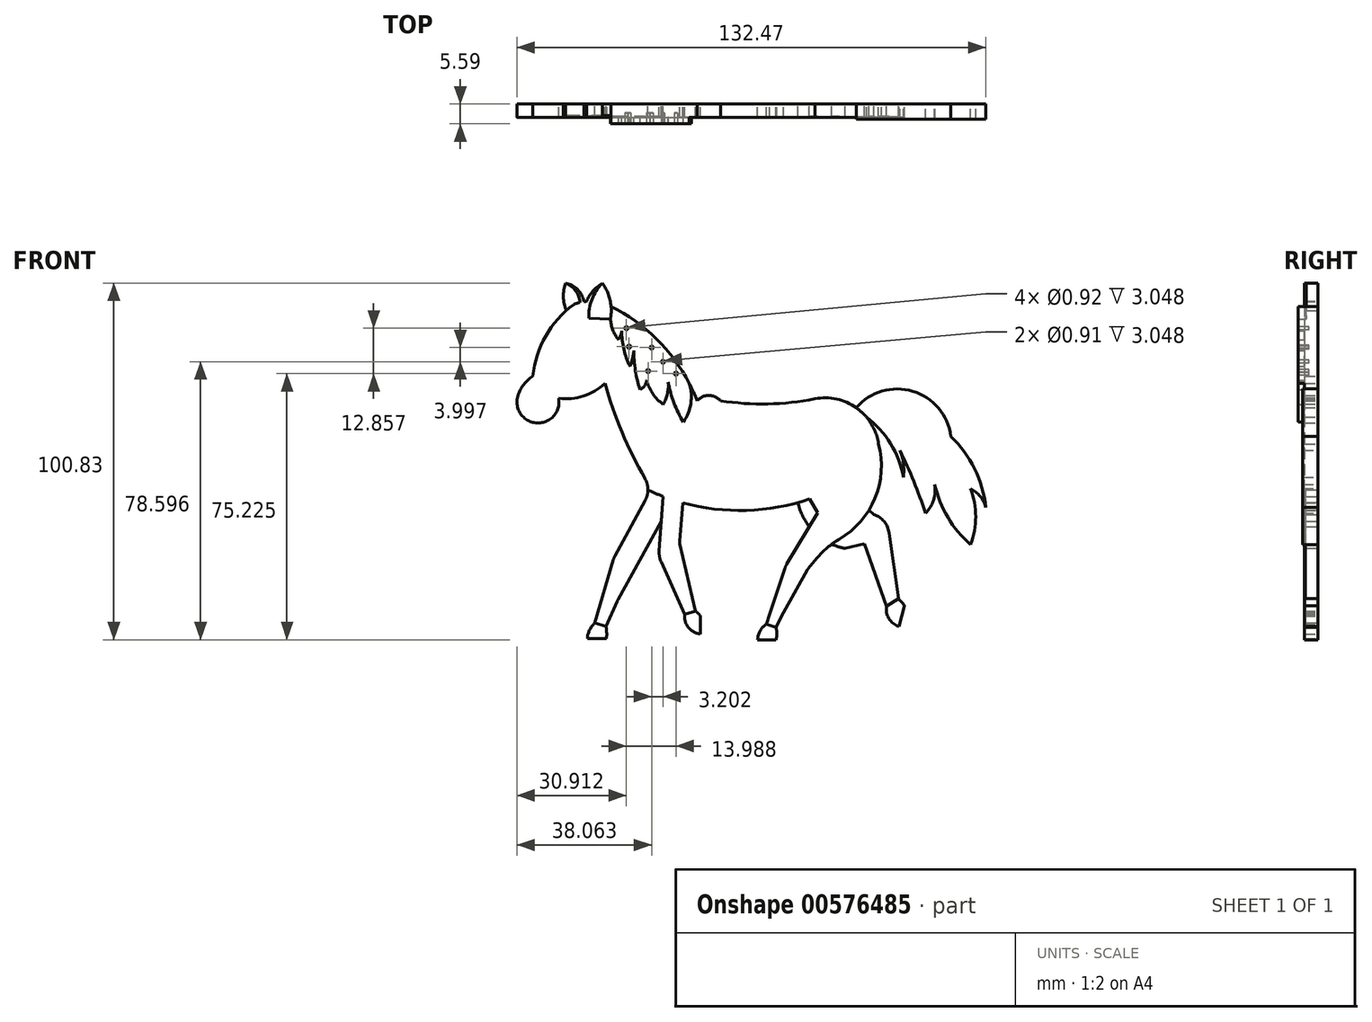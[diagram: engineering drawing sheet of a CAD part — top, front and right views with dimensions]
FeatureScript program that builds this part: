
annotation { "Feature Type Name" : "Feature", "Feature Type Description" : "" }
export const myFeature = defineFeature(function(context is Context, id is Id, definition is map)
    precondition{}
    {
        {
            var Q0;
            Q0=qCreatedBy(makeId("Front.planeOp"),FACE);
            var sketch = newSketch(context, id + "F0", { "sketchPlane" : qUnion([Q0])});
            skArc(sketch, "E0", {"start": v(-28.5, 3.23) * mm, "mid": v(-38.16, 18.83) * mm, "end": v(-52.8, 29.89) * mm});
            skArc(sketch, "E1", {"start": v(-21.88, 3.23) * mm, "mid": v(-25.19, 4.74) * mm, "end": v(-28.5, 3.23) * mm});
            skArc(sketch, "E2", {"start": v(-21.88, 3.23) * mm, "mid": v(-8.5, 2.33) * mm, "end": v(4.81, 3.8) * mm});
            skPoint(sketch, "E3.visualSharp", {"position": v(-35.88, -8.64) * mm});
            skArc(sketch, "E3.filletArc", {"start": v(-35.17, -11.7) * mm, "mid": v(-35.18, -11.7) * mm, "end": v(-35.18, -11.68) * mm});
            skPoint(sketch, "E4.visualSharp", {"position": v(-34.53, -14.51) * mm});
            skPoint(sketch, "E5.visualSharp", {"position": v(-52.4, -44.17) * mm});
            skPoint(sketch, "E6.visualSharp", {"position": v(-50.96, -53.17) * mm});
            skPoint(sketch, "E7.visualSharp", {"position": v(-50.4, -54.66) * mm});
            skPoint(sketch, "E8.visualSharp", {"position": v(-57.39, -59.58) * mm});
            skPoint(sketch, "E9.orphan", {"position": v(-27.47, -12) * mm});
            skArc(sketch, "E10", {"start": v(-67.62, 3.94) * mm, "mid": v(-57.44, 5.94) * mm, "end": v(-50.7, 13.82) * mm});
            skArc(sketch, "E11", {"start": v(-79.34, 3.55) * mm, "mid": v(-73.25, -3.06) * mm, "end": v(-67.62, 3.94) * mm});
            skArc(sketch, "E12", {"start": v(-74.9, 10.2) * mm, "mid": v(-77.82, 7.35) * mm, "end": v(-79.34, 3.55) * mm});
            skArc(sketch, "E13", {"start": v(-59.7, 31.32) * mm, "mid": v(-61.6, 31.02) * mm, "end": v(-63.44, 30.42) * mm});
            skArc(sketch, "E14", {"start": v(-63.44, 30.42) * mm, "mid": v(-71.29, 21.51) * mm, "end": v(-74.9, 10.2) * mm});
            skPoint(sketch, "E15.startSnap0", {"position": v(-57.44, 5.94) * mm});
            skArc(sketch, "E16", {"start": v(-43.23, -18.78) * mm, "mid": v(-49.7, -5.68) * mm, "end": v(-54.55, 8.11) * mm});
            skLineSegment(sketch, "E17", {"start": v(-43.16, -24.96) * mm, "end": v(-51.67, -40.58) * mm});
            skLineSegment(sketch, "E18", {"start": v(-52.18, -41.83) * mm, "end": v(-57.39, -59.58) * mm});
            skLineSegment(sketch, "E19", {"start": v(-38.6, -30.9) * mm, "end": v(-50.82, -52.92) * mm});
            skLineSegment(sketch, "E20", {"start": v(-51.07, -53.43) * mm, "end": v(-54.22, -60.52) * mm});
            skArc(sketch, "E21", {"start": v(-57.39, -59.58) * mm, "mid": v(-58.88, -61.57) * mm, "end": v(-59.5, -63.97) * mm});
            skLineSegment(sketch, "E22", {"start": v(-59.5, -63.97) * mm, "end": v(-54.08, -63.97) * mm});
            skArc(sketch, "E23", {"start": v(-54.08, -63.97) * mm, "mid": v(-54.05, -62.24) * mm, "end": v(-54.22, -60.52) * mm});
            skPoint(sketch, "E24.visualSharp", {"position": v(-51.99, -41.18) * mm});
            skArc(sketch, "E24.filletArc", {"start": v(-51.67, -40.58) * mm, "mid": v(-51.96, -41.2) * mm, "end": v(-52.18, -41.83) * mm});
            skArc(sketch, "E25.filletArc", {"start": v(-50.82, -52.92) * mm, "mid": v(-50.95, -53.17) * mm, "end": v(-51.07, -53.43) * mm});
            skPoint(sketch, "E26.visualSharp", {"position": v(-31.52, -18.16) * mm});
            skPoint(sketch, "E27.visualSharp", {"position": v(-41.44, -21.8) * mm});
            skArc(sketch, "E27.filletArc", {"start": v(-43.16, -24.96) * mm, "mid": v(-42.4, -21.86) * mm, "end": v(-43.23, -18.78) * mm});
            skArc(sketch, "E28", {"start": v(22.78, -8.96) * mm, "mid": v(16.5, 1.23) * mm, "end": v(4.81, 3.8) * mm});
            skArc(sketch, "E29", {"start": v(-42.4, -22) * mm, "mid": v(-40.25, -22.95) * mm, "end": v(-38.08, -23.82) * mm});
            skPoint(sketch, "E29.startSnap0", {"position": v(-42.4, -21.86) * mm});
            skLineSegment(sketch, "E30", {"start": v(-38.66, -42.3) * mm, "end": v(-32.03, -57.1) * mm});
            skLineSegment(sketch, "E31", {"start": v(-39.2, -39.25) * mm, "end": v(-38.08, -23.82) * mm});
            skArc(sketch, "E32.trimOffspring", {"start": v(-32.57, -25.62) * mm, "mid": v(-14.58, -27.77) * mm, "end": v(3.25, -24.53) * mm});
            skLineSegment(sketch, "E33", {"start": v(-32.57, -25.62) * mm, "end": v(-33.35, -36.4) * mm});
            skArc(sketch, "E34", {"start": v(-40.07, -8.18) * mm, "mid": v(-40.8, -16.22) * mm, "end": v(-38.08, -23.82) * mm});
            skArc(sketch, "E35", {"start": v(-32.57, -25.62) * mm, "mid": v(-31.52, -18.16) * mm, "end": v(-33.38, -10.86) * mm});
            skPoint(sketch, "E36.visualSharp", {"position": v(-39.32, -40.85) * mm});
            skArc(sketch, "E36.filletArc", {"start": v(-39.2, -39.25) * mm, "mid": v(-39.12, -40.81) * mm, "end": v(-38.66, -42.3) * mm});
            skPoint(sketch, "E37.visualSharp", {"position": v(-33.67, -40.85) * mm});
            skArc(sketch, "E37.filletArc", {"start": v(-33.35, -36.4) * mm, "mid": v(-33.37, -36.82) * mm, "end": v(-33.36, -37.24) * mm});
            skLineSegment(sketch, "E38", {"start": v(-28.96, -56.23) * mm, "end": v(-33.36, -37.24) * mm});
            skArc(sketch, "E39", {"start": v(-32.03, -57.1) * mm, "mid": v(-30.95, -60.84) * mm, "end": v(-27.52, -62.7) * mm});
            skLineSegment(sketch, "E40", {"start": v(-27.52, -62.7) * mm, "end": v(-27.52, -57.67) * mm});
            skArc(sketch, "E41", {"start": v(-27.52, -57.67) * mm, "mid": v(-28.18, -56.9) * mm, "end": v(-28.96, -56.23) * mm});
            skArc(sketch, "E42", {"start": v(-55.24, 36.49) * mm, "mid": v(-58.22, 31.92) * mm, "end": v(-59.04, 26.52) * mm});
            skPoint(sketch, "E43.orphan", {"position": v(-53.9, 30.42) * mm});
            skPoint(sketch, "E44.start.orphan", {"position": v(-52.24, 26.52) * mm});
            skArc(sketch, "E45", {"start": v(-52.98, 26.32) * mm, "mid": v(-53.07, 31.63) * mm, "end": v(-55.24, 36.49) * mm});
            skArc(sketch, "E46", {"start": v(-55.24, 36.49) * mm, "mid": v(-59.27, 32.24) * mm, "end": v(-60.51, 26.52) * mm});
            skArc(sketch, "E47", {"start": v(-61.6, 31.02) * mm, "mid": v(-62.84, 34.36) * mm, "end": v(-65.7, 36.49) * mm});
            skArc(sketch, "E48", {"start": v(-65.7, 36.49) * mm, "mid": v(-66.27, 32.6) * mm, "end": v(-65.46, 28.77) * mm});
            skArc(sketch, "E49", {"start": v(-60.51, 31.23) * mm, "mid": v(-62.26, 34.7) * mm, "end": v(-65.7, 36.49) * mm});
            skArc(sketch, "E50", {"start": v(5.3, 0) * mm, "mid": v(-0.54, -10.33) * mm, "end": v(1.75, -21.97) * mm});
            skLineSegment(sketch, "E51", {"start": v(5.36, -41.27) * mm, "end": v(2.9, -44.2) * mm});
            skLineSegment(sketch, "E52", {"start": v(2.68, -44.54) * mm, "end": v(-4.1, -56.69) * mm});
            skPoint(sketch, "E53.end.orphan", {"position": v(-8.88, -61.12) * mm});
            skPoint(sketch, "E53.start.orphan", {"position": v(-5.3, -56.69) * mm});
            skPoint(sketch, "E54.end.orphan", {"position": v(0, -44.36) * mm});
            skArc(sketch, "E55", {"start": v(11.65, -35.94) * mm, "mid": v(21.75, -24.32) * mm, "end": v(22.78, -8.96) * mm});
            skPoint(sketch, "E56.visualSharp", {"position": v(-2.59, -44.36) * mm});
            skPoint(sketch, "E57.visualSharp", {"position": v(2.78, -44.36) * mm});
            skArc(sketch, "E57.filletArc", {"start": v(2.9, -44.2) * mm, "mid": v(2.79, -44.37) * mm, "end": v(2.68, -44.54) * mm});
            skPoint(sketch, "E58.visualSharp", {"position": v(8.52, -37.48) * mm});
            skArc(sketch, "E58.filletArc", {"start": v(11.65, -35.94) * mm, "mid": v(8.27, -38.33) * mm, "end": v(5.36, -41.27) * mm});
            skPoint(sketch, "E59.visualSharp", {"position": v(9.47, -28.7) * mm});
            skPoint(sketch, "E60.visualSharp", {"position": v(-7.2, -56.69) * mm});
            skLineSegment(sketch, "E61", {"start": v(-6.19, -64.34) * mm, "end": v(-11.38, -64.34) * mm});
            skLineSegment(sketch, "E62", {"start": v(5.52, -28.42) * mm, "end": v(-3.13, -42.91) * mm});
            skLineSegment(sketch, "E63", {"start": v(-3.7, -44.17) * mm, "end": v(-8, -57.1) * mm});
            skPoint(sketch, "E56.filletArc.start.orphan", {"position": v(-1.93, -43.5) * mm});
            skPoint(sketch, "E64.visualSharp", {"position": v(-3.49, -43.5) * mm});
            skArc(sketch, "E64.filletArc", {"start": v(-3.13, -42.91) * mm, "mid": v(-3.45, -43.53) * mm, "end": v(-3.7, -44.17) * mm});
            skArc(sketch, "E65", {"start": v(-8.87, -59.93) * mm, "mid": v(-10.7, -61.8) * mm, "end": v(-11.38, -64.34) * mm});
            skArc(sketch, "E66", {"start": v(-6.2, -64.37) * mm, "mid": v(-5.95, -62.6) * mm, "end": v(-6.2, -60.82) * mm});
            skLineSegment(sketch, "E67", {"start": v(-8, -57.1) * mm, "end": v(-8.87, -59.93) * mm});
            skLineSegment(sketch, "E68", {"start": v(-6.2, -60.82) * mm, "end": v(-4.1, -56.69) * mm});
            skPoint(sketch, "E69.orphan", {"position": v(-3.18, -64.34) * mm});
            skLineSegment(sketch, "E70", {"start": v(1.75, -21.97) * mm, "end": v(5.52, -28.42) * mm});
            skPoint(sketch, "E71.orphan", {"position": v(5.52, -23.7) * mm});
            skArc(sketch, "E72", {"start": v(0, -25.54) * mm, "mid": v(1.2, -29.11) * mm, "end": v(3.18, -32.33) * mm});
            skArc(sketch, "E73.trimOffspring", {"start": v(9.55, -37.32) * mm, "mid": v(11.43, -38.04) * mm, "end": v(13.38, -38.52) * mm});
            skLineSegment(sketch, "E74", {"start": v(13.38, -38.52) * mm, "end": v(18.78, -37.2) * mm});
            skLineSegment(sketch, "E75", {"start": v(18.78, -37.2) * mm, "end": v(25.01, -54.82) * mm});
            skLineSegment(sketch, "E76", {"start": v(25.76, -34.1) * mm, "end": v(28.38, -52.73) * mm});
            skPoint(sketch, "E77.visualSharp", {"position": v(25.18, -29.96) * mm});
            skArc(sketch, "E77.filletArc", {"start": v(25.76, -34.1) * mm, "mid": v(24.35, -30.9) * mm, "end": v(21.46, -28.95) * mm});
            skLineSegment(sketch, "E78", {"start": v(21.46, -28.95) * mm, "end": v(20.03, -27.7) * mm});
            skArc(sketch, "E79", {"start": v(25.01, -54.82) * mm, "mid": v(25.7, -58.34) * mm, "end": v(28.51, -60.57) * mm});
            skLineSegment(sketch, "E80", {"start": v(28.51, -60.57) * mm, "end": v(30.16, -54.78) * mm});
            skArc(sketch, "E81", {"start": v(30.16, -54.78) * mm, "mid": v(29.33, -53.7) * mm, "end": v(28.38, -52.73) * mm});
            skLineSegment(sketch, "E82", {"start": v(-57.39, -59.58) * mm, "end": v(-54.22, -60.52) * mm});
            skLineSegment(sketch, "E83", {"start": v(-32.03, -57.1) * mm, "end": v(-28.96, -56.23) * mm});
            skLineSegment(sketch, "E84", {"start": v(-8.87, -59.93) * mm, "end": v(-6.2, -60.82) * mm});
            skLineSegment(sketch, "E85", {"start": v(25.01, -54.82) * mm, "end": v(28.38, -52.73) * mm});
            skLineSegment(sketch, "E86", {"start": v(-60.51, 26.52) * mm, "end": v(-59.04, 26.52) * mm});
            skLineSegment(sketch, "E87", {"start": v(-59.04, 26.52) * mm, "end": v(-52.98, 26.32) * mm});
            skArc(sketch, "E88", {"start": v(-52.98, 26.32) * mm, "mid": v(-52.3, 23.22) * mm, "end": v(-50.7, 20.49) * mm});
            skArc(sketch, "E89", {"start": v(-50.7, 20.49) * mm, "mid": v(-50.12, 21.68) * mm, "end": v(-49.78, 22.95) * mm});
            skArc(sketch, "E90", {"start": v(-49.78, 22.95) * mm, "mid": v(-49.2, 17.8) * mm, "end": v(-47.43, 12.93) * mm});
            skArc(sketch, "E91", {"start": v(-47.43, 12.93) * mm, "mid": v(-46.75, 15.12) * mm, "end": v(-46.37, 17.38) * mm});
            skArc(sketch, "E92", {"start": v(-46.37, 17.38) * mm, "mid": v(-45.93, 11.82) * mm, "end": v(-44.62, 6.4) * mm});
            skArc(sketch, "E93", {"start": v(-42.74, 9.07) * mm, "mid": v(-41.03, 5.23) * mm, "end": v(-38.1, 2.22) * mm});
            skArc(sketch, "E94", {"start": v(-38.1, 2.22) * mm, "mid": v(-36.86, 5.28) * mm, "end": v(-36.68, 8.58) * mm});
            skArc(sketch, "E95", {"start": v(-36.68, 8.58) * mm, "mid": v(-35.06, 2.68) * mm, "end": v(-32.37, -2.82) * mm});
            skArc(sketch, "E96", {"start": v(-32.37, -2.82) * mm, "mid": v(-30.27, 2.45) * mm, "end": v(-30.7, 8.1) * mm});
            skArc(sketch, "E97", {"start": v(-44.62, 6.4) * mm, "mid": v(-43.31, 7.48) * mm, "end": v(-42.74, 9.07) * mm});
            skArc(sketch, "E98", {"start": v(29.78, -18.35) * mm, "mid": v(29.81, -14.53) * mm, "end": v(28.82, -10.84) * mm});
            skArc(sketch, "E99", {"start": v(36.04, -28.56) * mm, "mid": v(32.74, -19.57) * mm, "end": v(28.82, -10.84) * mm});
            skArc(sketch, "E100", {"start": v(36.04, -28.56) * mm, "mid": v(38.32, -24.84) * mm, "end": v(38.66, -20.48) * mm});
            skArc(sketch, "E101", {"start": v(38.66, -20.48) * mm, "mid": v(42.37, -29.75) * mm, "end": v(48.75, -37.42) * mm});
            skArc(sketch, "E102", {"start": v(48.75, -37.42) * mm, "mid": v(50.24, -29.53) * mm, "end": v(48.75, -21.63) * mm});
            skArc(sketch, "E103", {"start": v(53.09, -26.92) * mm, "mid": v(51.5, -23.8) * mm, "end": v(48.75, -21.63) * mm});
            skArc(sketch, "E104", {"start": v(43.17, -6.8) * mm, "mid": v(32.45, 5.91) * mm, "end": v(16.5, 1.23) * mm});
            skArc(sketch, "E105", {"start": v(53.09, -26.92) * mm, "mid": v(49.91, -15.98) * mm, "end": v(43.17, -6.8) * mm});
            skArc(sketch, "E106", {"start": v(29.78, -18.35) * mm, "mid": v(26.21, -8.88) * mm, "end": v(19.36, -1.41) * mm});
            skCircle(sketch, "E107", {"center": v(5.22, 54.47) * mm, "radius": 8.7 * mm});
            skSolve(sketch);
        }
        {
            var Q0;
            Q0=makeQuery(id+"F0.imprint","IMPRINT",FACE,{"disambiguationData":[TD([[makeQuery(id+"F0.imprint","IMPRINT",EDGE,{"derivedFrom":sQuery(id+"F0.wireOp",EDGE,"E21")}),1.0]])]});
            extrude(context, id + "F1", {"entities" : qUnion([Q0]), "depth" : 3.8 * mm, "offsetDistance" : 25.4 * mm});
        }
        {
            var Q0;
            Q0=makeQuery(id+"F0.imprint","IMPRINT",FACE,{"disambiguationData":[TD([[makeQuery(id+"F0.imprint","IMPRINT",EDGE,{"derivedFrom":sQuery(id+"F0.wireOp",EDGE,"E39")}),1.0]])]});
            extrude(context, id + "F2", {"entities" : qUnion([Q0]), "depth" : 3.8 * mm, "offsetDistance" : 25.4 * mm});
        }
        {
            var Q0;
            {var subQ0=sQuery(id+"F0.wireOp",EDGE,"E61");Q0=makeQuery(id+"F0.imprint","IMPRINT",FACE,{"disambiguationData":[TD([[makeQuery(id+"F0.imprint","IMPRINT",EDGE,{"derivedFrom":subQ0}),-1.0]])]});}
            extrude(context, id + "F3", {"entities" : qUnion([Q0]), "depth" : 3.8 * mm, "offsetDistance" : 25.4 * mm});
        }
        {
            var Q0;
            Q0=makeQuery(id+"F0.imprint","IMPRINT",FACE,{"disambiguationData":[TD([[makeQuery(id+"F0.imprint","IMPRINT",EDGE,{"derivedFrom":sQuery(id+"F0.wireOp",EDGE,"E79")}),1.0]])]});
            extrude(context, id + "F4", {"entities" : qUnion([Q0]), "depth" : 3.8 * mm, "offsetDistance" : 25.4 * mm});
        }
        {
            var Q0;
            {var subQ0=sQuery(id+"F0.wireOp",EDGE,"E73.trimOffspring");Q0=makeQuery(id+"F0.imprint","IMPRINT",FACE,{"disambiguationData":[TD([[makeQuery(id+"F0.imprint","IMPRINT",EDGE,{"derivedFrom":subQ0}),1.0]])]});}
            extrude(context, id + "F5", {"entities" : qUnion([Q0]), "operationType" : NewBodyOperationType.ADD, "depth" : 3.56 * mm, "offsetDistance" : 25.4 * mm});
        }
        {
            var Q0;
            {var subQ2=sQuery(id+"F0.wireOp",EDGE,"E17");Q0=makeQuery(id+"F0.imprint","IMPRINT",FACE,{"disambiguationData":[TD([[makeQuery(id+"F0.imprint","IMPRINT",EDGE,{"derivedFrom":subQ2}),1.0]])]});}
            extrude(context, id + "F6", {"entities" : qUnion([Q0]), "depth" : 3.56 * mm, "offsetDistance" : 25.4 * mm});
        }
        {
            var Q0;
            {var subQ32=sQuery(id+"F0.wireOp",EDGE,"E1");Q0=makeQuery(id+"F0.imprint","IMPRINT",FACE,{"disambiguationData":[TD([[makeQuery(id+"F0.imprint","IMPRINT",EDGE,{"derivedFrom":subQ32}),1.0]])]});}
            extrude(context, id + "F7", {"entities" : qUnion([Q0]), "depth" : 3.8 * mm, "offsetDistance" : 25.4 * mm});
        }
        {
            var Q0;
            {var subQ0=sQuery(id+"F0.wireOp",EDGE,"E47");Q0=makeQuery(id+"F0.imprint","IMPRINT",FACE,{"disambiguationData":[TD([[makeQuery(id+"F0.imprint","IMPRINT",EDGE,{"derivedFrom":subQ0}),-1.0]])]});}
            extrude(context, id + "F8", {"entities" : qUnion([Q0]), "operationType" : NewBodyOperationType.ADD, "depth" : 3.8 * mm, "offsetDistance" : 25.4 * mm});
        }
        {
            var Q0;
            {var subQ0=sQuery(id+"F0.wireOp",EDGE,"E42");Q0=makeQuery(id+"F0.imprint","IMPRINT",FACE,{"disambiguationData":[TD([[makeQuery(id+"F0.imprint","IMPRINT",EDGE,{"derivedFrom":subQ0}),-1.0]])]});}
            extrude(context, id + "F9", {"entities" : qUnion([Q0]), "operationType" : NewBodyOperationType.ADD, "depth" : 3.8 * mm, "offsetDistance" : 25.4 * mm});
        }
        {
            var Q0;
            {var subQ3=sQuery(id+"F0.wireOp",EDGE,"E47");Q0=makeQuery(id+"F0.imprint","IMPRINT",FACE,{"disambiguationData":[TD([[makeQuery(id+"F0.imprint","IMPRINT",EDGE,{"derivedFrom":subQ3}),1.0]])]});}
            extrude(context, id + "F10", {"entities" : qUnion([Q0]), "operationType" : NewBodyOperationType.ADD, "depth" : 3.3 * mm, "offsetDistance" : 25.4 * mm});
        }
        {
            var Q0;
            {var subQ0=sQuery(id+"F0.wireOp",EDGE,"E42");Q0=makeQuery(id+"F0.imprint","IMPRINT",FACE,{"disambiguationData":[TD([[makeQuery(id+"F0.imprint","IMPRINT",EDGE,{"derivedFrom":subQ0}),1.0]])]});}
            extrude(context, id + "F11", {"entities" : qUnion([Q0]), "operationType" : NewBodyOperationType.ADD, "depth" : 3.3 * mm, "offsetDistance" : 25.4 * mm});
        }
        {
            var Q0;
            {var subQ3=sQuery(id+"F0.wireOp",EDGE,"E72");Q0=makeQuery(id+"F0.imprint","IMPRINT",FACE,{"disambiguationData":[TD([[makeQuery(id+"F0.imprint","IMPRINT",EDGE,{"derivedFrom":subQ3}),1.0]])]});}
            extrude(context, id + "F12", {"entities" : qUnion([Q0]), "operationType" : NewBodyOperationType.ADD, "depth" : 3.56 * mm, "offsetDistance" : 25.4 * mm});
        }
        {
            var Q0;
            {var subQ3=sQuery(id+"F0.wireOp",EDGE,"E88");Q0=makeQuery(id+"F0.imprint","IMPRINT",FACE,{"disambiguationData":[TD([[makeQuery(id+"F0.imprint","IMPRINT",EDGE,{"derivedFrom":subQ3}),1.0]])]});}
            extrude(context, id + "F13", {"entities" : qUnion([Q0]), "operationType" : NewBodyOperationType.ADD, "depth" : 5.6 * mm, "offsetDistance" : 25.4 * mm});
        }
        {
            var Q0;
            Q0=makeQuery(id+"F0.imprint","IMPRINT",FACE,{"disambiguationData":[TD([[makeQuery(id+"F0.imprint","IMPRINT",EDGE,{"derivedFrom":sQuery(id+"F0.wireOp",EDGE,"E98")}),1.0]])]});
            extrude(context, id + "F14", {"entities" : qUnion([Q0]), "operationType" : NewBodyOperationType.ADD, "depth" : 4.32 * mm, "offsetDistance" : 25.4 * mm});
        }
        {
            var Q0;
            Q0=makeQuery(id+"F13.opExtrude","CAP_FACE",FACE,{"disambiguationData":[OSD([sQuery(id+"F0.wireOp",EDGE,"E0"),sQuery(id+"F0.wireOp",EDGE,"E45"),sQuery(id+"F0.wireOp",EDGE,"E88"),sQuery(id+"F0.wireOp",EDGE,"E89"),sQuery(id+"F0.wireOp",EDGE,"E90"),sQuery(id+"F0.wireOp",EDGE,"E91"),sQuery(id+"F0.wireOp",EDGE,"E92"),sQuery(id+"F0.wireOp",EDGE,"E93"),sQuery(id+"F0.wireOp",EDGE,"E94"),sQuery(id+"F0.wireOp",EDGE,"E95"),sQuery(id+"F0.wireOp",EDGE,"E96"),sQuery(id+"F0.wireOp",EDGE,"E97")])],"isStart":false});
            var sketch = newSketch(context, id + "F15", { "sketchPlane" : qUnion([Q0])});
            skCircle(sketch, "E108", {"center": v(-48.47, 23.74) * mm, "radius": 0.46 * mm});
            skCircle(sketch, "E109", {"center": v(-47.72, 18.52) * mm, "radius": 0.46 * mm});
            skCircle(sketch, "E110", {"center": v(-41.32, 18.25) * mm, "radius": 0.45 * mm});
            skCircle(sketch, "E111", {"center": v(-42.35, 11.63) * mm, "radius": 0.46 * mm});
            skCircle(sketch, "E112", {"center": v(-38.77, 5.9) * mm, "radius": 0.46 * mm});
            skCircle(sketch, "E113", {"center": v(-34.48, 10.88) * mm, "radius": 0.46 * mm});
            skCircle(sketch, "E114", {"center": v(-38.12, 14.26) * mm, "radius": 0.45 * mm});
            skSolve(sketch);
        }
        {
            var Q0;
            Q0=makeQuery(id+"F15.imprint","IMPRINT",FACE,{"disambiguationData":[TD([[makeQuery(id+"F15.imprint","IMPRINT",EDGE,{"derivedFrom":sQuery(id+"F15.wireOp",EDGE,"E108")}),1.0]])]});
            extrude(context, id + "F16", {"entities" : qUnion([Q0]), "operationType" : NewBodyOperationType.REMOVE, "oppositeDirection" : true, "depth" : 3.05 * mm, "offsetDistance" : 25.4 * mm});
        }
        {
            var Q0;
            Q0=makeQuery(id+"F15.imprint","IMPRINT",FACE,{"disambiguationData":[TD([[makeQuery(id+"F15.imprint","IMPRINT",EDGE,{"derivedFrom":sQuery(id+"F15.wireOp",EDGE,"E109")}),1.0]])]});
            var Q1;
            Q1=makeQuery(id+"F15.imprint","IMPRINT",FACE,{"disambiguationData":[TD([[makeQuery(id+"F15.imprint","IMPRINT",EDGE,{"derivedFrom":sQuery(id+"F15.wireOp",EDGE,"E110")}),1.0]])]});
            var Q2;
            Q2=makeQuery(id+"F15.imprint","IMPRINT",FACE,{"disambiguationData":[TD([[makeQuery(id+"F15.imprint","IMPRINT",EDGE,{"derivedFrom":sQuery(id+"F15.wireOp",EDGE,"E111")}),1.0]])]});
            var Q3;
            Q3=makeQuery(id+"F15.imprint","IMPRINT",FACE,{"disambiguationData":[TD([[makeQuery(id+"F15.imprint","IMPRINT",EDGE,{"derivedFrom":sQuery(id+"F15.wireOp",EDGE,"E114")}),1.0]])]});
            var Q4;
            Q4=makeQuery(id+"F15.imprint","IMPRINT",FACE,{"disambiguationData":[TD([[makeQuery(id+"F15.imprint","IMPRINT",EDGE,{"derivedFrom":sQuery(id+"F15.wireOp",EDGE,"E113")}),1.0]])]});
            extrude(context, id + "F17", {"entities" : qUnion([Q0, Q1, Q2, Q3, Q4]), "operationType" : NewBodyOperationType.REMOVE, "oppositeDirection" : true, "depth" : 3.05 * mm, "offsetDistance" : 25.4 * mm});
        }
    });
